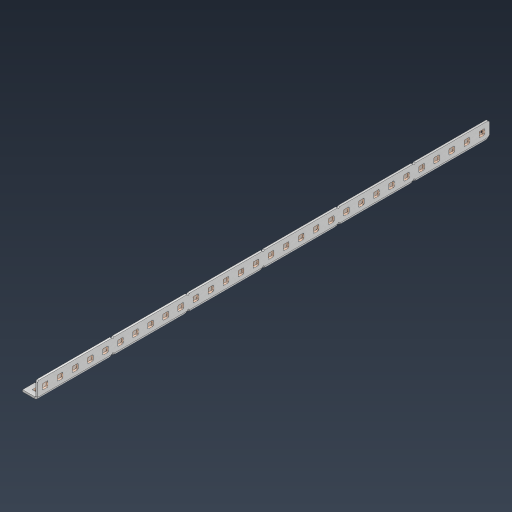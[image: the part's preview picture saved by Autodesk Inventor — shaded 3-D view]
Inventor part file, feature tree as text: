
AUTODESK INVENTOR PART (.ipt)
format: ipt  version: 2024.3 (Build 283343000, 343)  size: 1,141,760 bytes
history: native  units: in
note: dims shown in document units (in); Inventor stores cm internally (conversion verified against a paired STEP export)
features: other x97, extrude x88, sheet_metal_op x11, pattern_linear x2, mirror x1, chamfer x1, sketch x1
ambient origin geometry x8: Origin, YZ Plane, XZ Plane, XY Plane, X Axis, Y Axis, Z Axis, Center Point
bodies: Solid1 (feature_tree), Body (feature_tree)
feature tree (201):
  sheet_metal_op  "Flanges"
  other  "Flange Pattern Plane"
  other  "Flange Pattern Sketch"
  sheet_metal_op  "Flange Pattern"
  sheet_metal_op  "Body Pattern"
  pattern_linear  "Center Pattern"  Spacing1=15.0in  [1 undecoded]
  other  "Arc Length"
  mirror  "Notch Mirror"
  pattern_linear  "Notch Pattern"  Spacing1=0.0625in  [1 undecoded]
  chamfer  "End Chamfer"
  extrude  "Half Cut"  Depth=0.0625in
  other  "Plate1"
  sketch  "Sketch2"  dims[d0=1.0in d1=15.0in d2=0.0625in d3=0.0625in d4=0.0312in d5=0.125in d6=0.0625in d7=0.5in d8=90.0deg d9=0.0312in d10=0.25in d11=0.0625in d12=0.0625in d16=0.182in d17=0.02in d18=0.0625in d19=0.0in d20=0.25in d21=0.25in d38=11.811in d40=0.5in d41=0.3937in d43=1.0in d46=0.172in d47=1.0in d48=0.0in d49=0.182in d50=0.02in d51=0.25in d52=0.25in d53=0.0625in d54=0.0in d55=0.172in d56=1.0in d57=0.0in d58=0.25in d60=11.811in d62=0.5in d63=0.3937in d65=0.5in d85=0.1473in d86=0.1782in d88=0.04in d89=0.0625in d90=0.0in d91=0.04in d92=0.0491in d95=2.5in d96=0.04in d97=0.25in d98=45.0deg d99=0.25in d100=0.5in d101=0.0in d102=2.497in d106=0.182in d107=0.02in d108=0.5in d109=0.5in d110=0.0625in d111=0.0in d112=0.172in d113=0.5in d114=0.0in d117=0.5in d118=0.5in d119=0.5in]
  other  "Plate2"
  sheet_metal_op  "Bend1"
  sheet_metal_op  "Corner1"
  other  "Srf1"
  other  "Srf2"
  other  "Srf91"
  sheet_metal_op  "Body Pattern Sketch"
  other  "Srf92"
  other  "Srf786"
  other  "Srf823"
  other  "Srf824"
  other  "Srf825"
  other  "Srf826"
  other  "Srf827"
  other  "Srf828"
  other  "Srf829"
  other  "Srf856"
  other  "Srf857"
  other  "Srf858"
  other  "Srf859"
  other  "Srf860"
  other  "Srf861"
  other  "Srf862"
  other  "Srf889"
  other  "Srf890"
  other  "Srf891"
  other  "Srf892"
  other  "Srf893"
  other  "Srf894"
  other  "Srf895"
  other  "Srf896"
  other  "Srf922"
  other  "Srf923"
  other  "Srf924"
  other  "Srf925"
  other  "Srf926"
  other  "Srf959"
  other  "Srf960"
  other  "Srf961"
  other  "Srf962"
  other  "Srf963"
  other  "Srf996"
  other  "Srf997"
  other  "Srf998"
  other  "Srf999"
  other  "Srf1000"
  other  "Srf1143"
  other  "Srf1144"
  other  "Srf1145"
  other  "Srf1146"
  other  "Srf1147"
  other  "Srf1148"
  other  "Srf1149"
  other  "Srf1150"
  other  "Srf1151"
  other  "Srf1152"
  other  "Srf1153"
  other  "Srf1154"
  other  "Srf1155"
  other  "Srf1156"
  other  "Srf1157"
  other  "Srf1158"
  other  "Srf1199"
  other  "Srf1200"
  other  "Srf1201"
  other  "Srf1202"
  other  "Srf1203"
  other  "Srf1204"
  other  "Srf1205"
  other  "Srf1206"
  other  "Srf1207"
  other  "Srf1208"
  other  "Srf1209"
  other  "Srf1210"
  other  "Srf1211"
  other  "Srf1212"
  other  "Srf1213"
  other  "Srf1214"
  other  "Srf1255"
  other  "Srf1256"
  other  "Srf1257"
  other  "Srf1258"
  other  "Srf1259"
  other  "Srf1260"
  other  "Srf1261"
  other  "Srf1262"
  other  "Srf1263"
  other  "Srf1264"
  other  "Srf1265"
  other  "Srf1266"
  other  "Srf1267"
  other  "Srf1268"
  other  "Srf1269"
  other  "Srf1270"
  sheet_metal_op  "Flange Stamp"
  sheet_metal_op  "Flange Circle"
  sheet_metal_op  "Body Stamp"
  sheet_metal_op  "Body Circle"
  other  "Center Stamp"
  other  "Center Circle"
  sheet_metal_op  "Notch"
  extrude  "ExtrusionSrf2"  Depth=0.0312in
  extrude  "ExtrusionSrf92"  Depth=0.5in
  extrude  "ExtrusionSrf823"  Depth=0.0625in
  extrude  "ExtrusionSrf824"  Depth=0.5in TaperAngle=90.0deg
  extrude  "ExtrusionSrf825"  Depth=0.25in
  extrude  "ExtrusionSrf826"  Depth=0.0625in
  extrude  "ExtrusionSrf827"  Depth=0.0625in
  extrude  "ExtrusionSrf828"  Depth=0.182in
  extrude  "ExtrusionSrf829"  Depth=0.02in
  extrude  "ExtrusionSrf856"  Depth=0.0625in
  extrude  "ExtrusionSrf857"  TaperAngle=0.0deg  [1 undecoded]
  extrude  "ExtrusionSrf858"  Depth=0.25in
  extrude  "ExtrusionSrf859"  Depth=0.25in
  extrude  "ExtrusionSrf860"  Depth=0.5in
  extrude  "ExtrusionSrf861"  Depth=0.5in
  extrude  "ExtrusionSrf862"  Depth=1.0in TaperAngle=0.0deg
  extrude  "ExtrusionSrf889"  Depth=0.182in
  extrude  "ExtrusionSrf890"  Depth=0.02in
  extrude  "ExtrusionSrf891"  Depth=0.25in
  extrude  "ExtrusionSrf892"  Depth=0.25in
  extrude  "ExtrusionSrf893"  Depth=0.0625in
  extrude  "ExtrusionSrf894"  TaperAngle=0.0deg  [1 undecoded]
  extrude  "ExtrusionSrf895"  Depth=0.5in
  extrude  "ExtrusionSrf896"  Depth=1.0in TaperAngle=0.0deg
  extrude  "ExtrusionSrf922"  Depth=0.25in
  extrude  "ExtrusionSrf923"  Depth=0.5in
  extrude  "ExtrusionSrf924"  Depth=0.5in
  extrude  "ExtrusionSrf925"  Depth=0.5in
  extrude  "ExtrusionSrf926"  Depth=0.5in
  extrude  "ExtrusionSrf959"  Depth=0.5in
  extrude  "ExtrusionSrf960"  Depth=0.0625in
  extrude  "ExtrusionSrf961"  TaperAngle=0.0deg  [1 undecoded]
  extrude  "ExtrusionSrf962"  Depth=0.5in
  extrude  "ExtrusionSrf963"  Depth=0.5in
  extrude  "ExtrusionSrf996"  Depth=2.5in
  extrude  "ExtrusionSrf997"  Depth=0.25in TaperAngle=45.0deg
  extrude  "ExtrusionSrf998"  Depth=0.25in
  extrude  "ExtrusionSrf999"  Depth=0.5in TaperAngle=0.0deg
  extrude  "ExtrusionSrf1000"  Depth=0.5in
  extrude  "ExtrusionSrf1143"  Depth=0.182in
  extrude  "ExtrusionSrf1144"  Depth=0.02in
  extrude  "ExtrusionSrf1145"  Depth=0.5in
  extrude  "ExtrusionSrf1146"  Depth=0.5in
  extrude  "ExtrusionSrf1147"  Depth=0.0625in
  extrude  "ExtrusionSrf1148"  TaperAngle=0.0deg  [1 undecoded]
  extrude  "ExtrusionSrf1149"  Depth=0.5in
  extrude  "ExtrusionSrf1150"  Depth=0.5in TaperAngle=0.0deg
  extrude  "ExtrusionSrf1151"  Depth=0.5in
  extrude  "ExtrusionSrf1152"  Depth=0.5in
  extrude  "ExtrusionSrf1153"  Depth=0.5in
  extrude  "ExtrusionSrf1154"  [1 undecoded]
  extrude  "ExtrusionSrf1155"  [1 undecoded]
  extrude  "ExtrusionSrf1156"  [1 undecoded]
  extrude  "ExtrusionSrf1157"  [1 undecoded]
  extrude  "ExtrusionSrf1158"  [1 undecoded]
  extrude  "ExtrusionSrf1199"  [1 undecoded]
  extrude  "ExtrusionSrf1200"  [1 undecoded]
  extrude  "ExtrusionSrf1201"  [1 undecoded]
  extrude  "ExtrusionSrf1202"  [1 undecoded]
  extrude  "ExtrusionSrf1203"  [1 undecoded]
  extrude  "ExtrusionSrf1204"  [1 undecoded]
  extrude  "ExtrusionSrf1205"  [1 undecoded]
  extrude  "ExtrusionSrf1206"  [1 undecoded]
  extrude  "ExtrusionSrf1207"  [1 undecoded]
  extrude  "ExtrusionSrf1208"  [1 undecoded]
  extrude  "ExtrusionSrf1209"  [1 undecoded]
  extrude  "ExtrusionSrf1210"  [1 undecoded]
  extrude  "ExtrusionSrf1211"  [1 undecoded]
  extrude  "ExtrusionSrf1212"  [1 undecoded]
  extrude  "ExtrusionSrf1213"  [1 undecoded]
  extrude  "ExtrusionSrf1214"  [1 undecoded]
  extrude  "ExtrusionSrf1255"  [1 undecoded]
  extrude  "ExtrusionSrf1256"  [1 undecoded]
  extrude  "ExtrusionSrf1257"  [1 undecoded]
  extrude  "ExtrusionSrf1258"  [1 undecoded]
  extrude  "ExtrusionSrf1259"  [1 undecoded]
  extrude  "ExtrusionSrf1260"  [1 undecoded]
  extrude  "ExtrusionSrf1261"  [1 undecoded]
  extrude  "ExtrusionSrf1262"  [1 undecoded]
  extrude  "ExtrusionSrf1263"  [1 undecoded]
  extrude  "ExtrusionSrf1264"  [1 undecoded]
  extrude  "ExtrusionSrf1265"  [1 undecoded]
  extrude  "ExtrusionSrf1266"  [1 undecoded]
  extrude  "ExtrusionSrf1267"  [1 undecoded]
  extrude  "ExtrusionSrf1268"  [1 undecoded]
  extrude  "ExtrusionSrf1269"  [1 undecoded]
  extrude  "ExtrusionSrf1270"  [1 undecoded]
note: 43 required parameter values undecoded (feature->parameter linkage not recoverable at this tier; creation-order binding heuristic only, values carry confidence <= 0.55)
